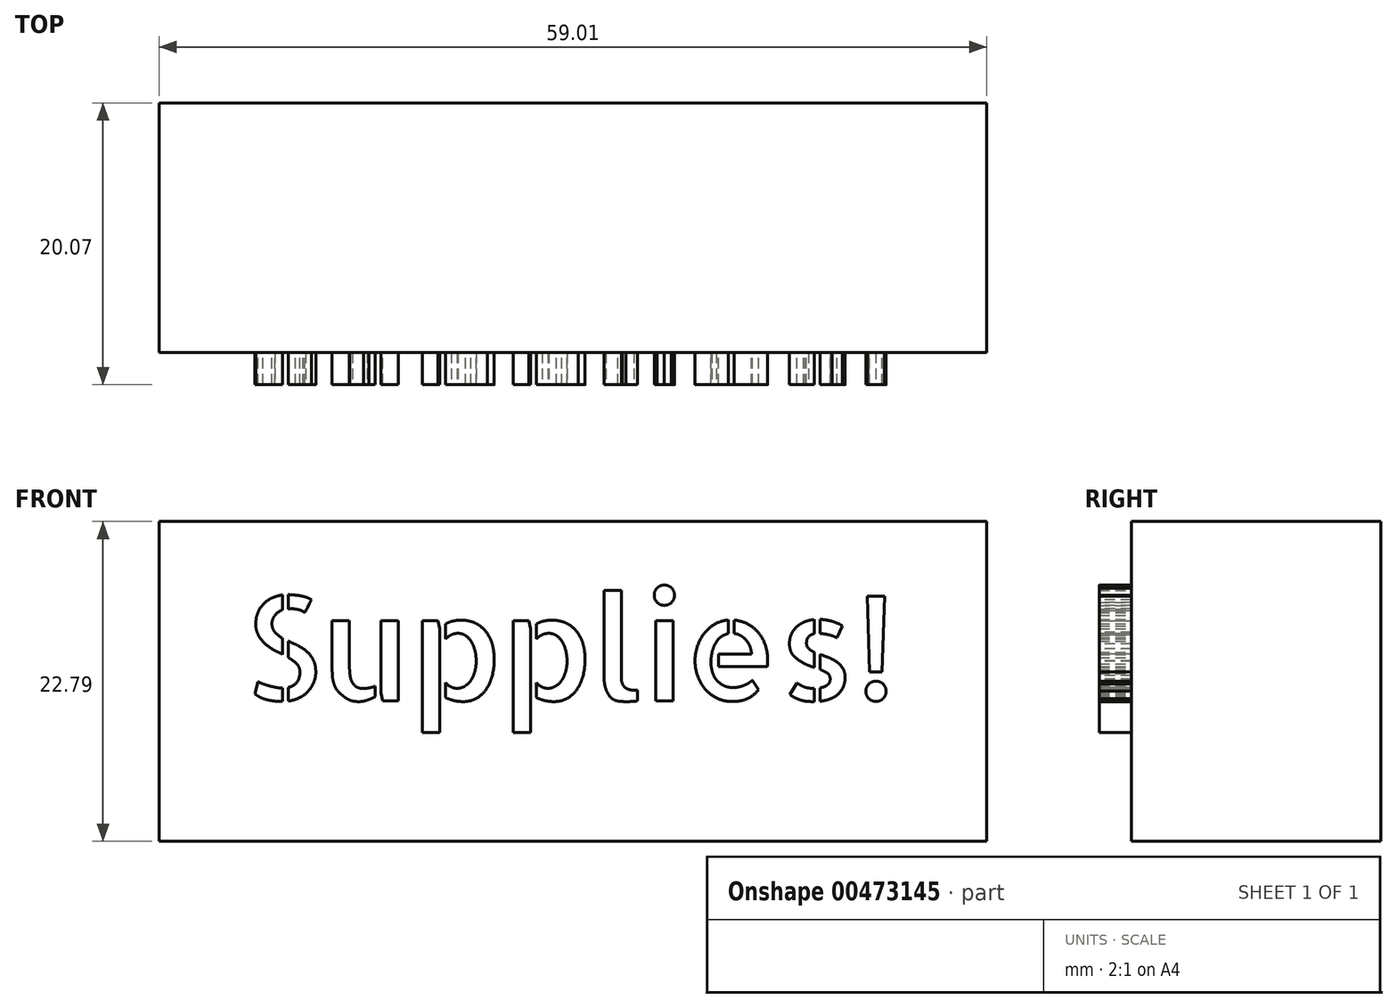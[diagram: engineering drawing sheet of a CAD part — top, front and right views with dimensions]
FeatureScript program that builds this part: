
annotation { "Feature Type Name" : "Feature", "Feature Type Description" : "" }
export const myFeature = defineFeature(function(context is Context, id is Id, definition is map)
    precondition{}
    {
        {
            var Q0;
            Q0=qCreatedBy(makeId("Front.planeOp"),FACE);
            var sketch = newSketch(context, id + "F0", { "sketchPlane" : qUnion([Q0])});
            skLineSegment(sketch, "E0.bottom", {"start": v(-49.33, 41.52) * mm, "end": v(9.68, 41.52) * mm});
            skLineSegment(sketch, "E0.top", {"start": v(-49.33, 18.73) * mm, "end": v(9.68, 18.73) * mm});
            skLineSegment(sketch, "E0.left", {"start": v(-49.33, 41.52) * mm, "end": v(-49.33, 18.73) * mm});
            skLineSegment(sketch, "E0.right", {"start": v(9.68, 41.52) * mm, "end": v(9.68, 18.73) * mm});
            skSolve(sketch);
        }
        {
            var Q0;
            Q0=qCreatedBy(makeId("Front.planeOp"),FACE);
            var sketch = newSketch(context, id + "F1", { "sketchPlane" : qUnion([Q0])});
            skText(sketch, "E1", { "text": "Supplies!", "fontName": "AllertaStencil-Regular.ttf"});
            const initialGuessF1  = {"E1": [-0.04331, 0.02873, 1, 0, 0.00746]};
            skSetInitialGuess(sketch, initialGuessF1);
            skSolve(sketch);
        }
        {
            var Q0;
            Q0 = qSketchRegion(id + "F0", true);
            extrude(context, id + "F2", {"entities" : qUnion([Q0]), "depth" : 17.78 * mm});
        }
        {
            var Q0;
            Q0 = qSketchRegion(id + "F1", true);
            extrude(context, id + "F3", {"entities" : qUnion([Q0]), "operationType" : NewBodyOperationType.ADD, "depth" : 20.07 * mm});
        }
    });
